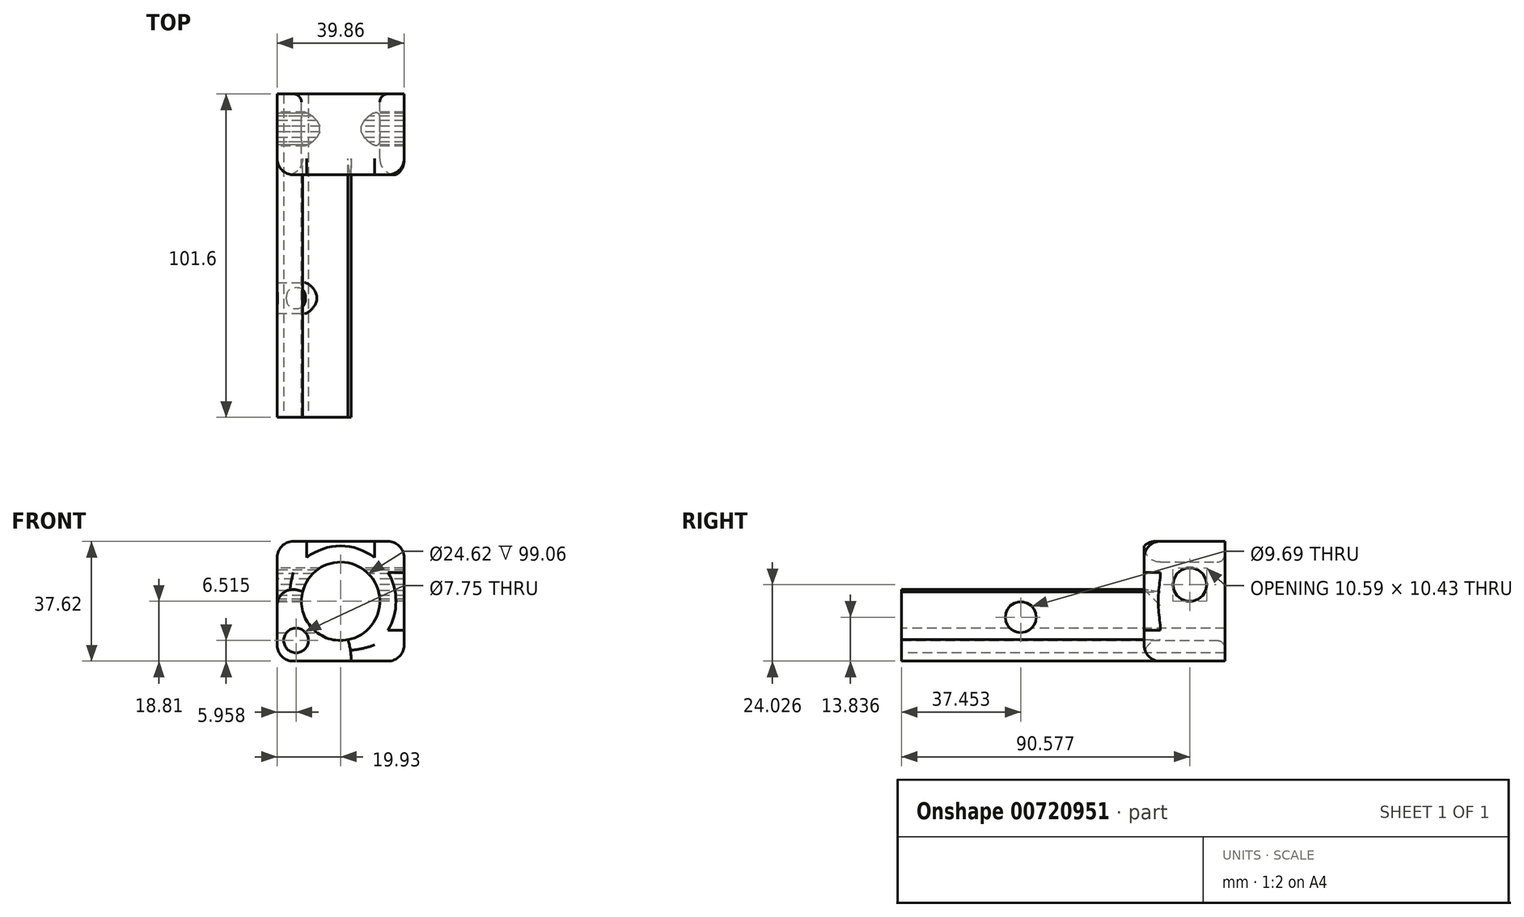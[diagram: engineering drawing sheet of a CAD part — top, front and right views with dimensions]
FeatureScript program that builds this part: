
annotation { "Feature Type Name" : "Feature", "Feature Type Description" : "" }
export const myFeature = defineFeature(function(context is Context, id is Id, definition is map)
    precondition{}
    {
        {
            var Q0;
            Q0=qCreatedBy(makeId("Front.planeOp"),FACE);
            var sketch = newSketch(context, id + "F0", { "sketchPlane" : qUnion([Q0])});
            skCircle(sketch, "E0", {"center": v(0, 0) * mm, "radius": 12.3 * mm});
            skLineSegment(sketch, "E1.bottom", {"start": v(-19.93, 18.81) * mm, "end": v(19.93, 18.81) * mm});
            skLineSegment(sketch, "E1.top", {"start": v(-19.93, -18.81) * mm, "end": v(19.93, -18.81) * mm});
            skLineSegment(sketch, "E1.left", {"start": v(-19.93, 18.81) * mm, "end": v(-19.93, -18.81) * mm});
            skLineSegment(sketch, "E1.right", {"start": v(19.93, 18.81) * mm, "end": v(19.93, -18.81) * mm});
            skCircle(sketch, "E2", {"center": v(-19.93, -18.81) * mm, "radius": 23.26 * mm});
            skSolve(sketch);
        }
        {
            var Q0;
            Q0=makeQuery(id+"F0.imprint","IMPRINT",FACE,{"disambiguationData":[TD([[makeQuery(id+"F0.imprint","IMPRINT",EDGE,{"derivedFrom":sQuery(id+"F0.wireOp",EDGE,"E0")}),-1.0]])]});
            extrude(context, id + "F1", {"entities" : qUnion([Q0]), "depth" : 101.6 * mm, "offsetDistance" : 25.4 * mm});
        }
        {
            var Q0;
            {var subQ1=sQuery(id+"F0.wireOp",EDGE,"E1.bottom");Q0=makeQuery(id+"F0.imprint","IMPRINT",FACE,{"disambiguationData":[TD([[makeQuery(id+"F0.imprint","IMPRINT",EDGE,{"derivedFrom":subQ1}),-1.0]])]});}
            extrude(context, id + "F2", {"entities" : qUnion([Q0]), "operationType" : NewBodyOperationType.ADD, "depth" : 25.4 * mm, "offsetDistance" : 25.4 * mm});
        }
        {
            var Q0;
            Q0=makeQuery(id+"F2.opExtrude","SWEPT_EDGE",EDGE,{"disambiguationData":[OSD([sQuery(id+"F0.wireOp",EDGE,"E1.bottom"),sQuery(id+"F0.wireOp",EDGE,"E1.left")])]});
            var Q1;
            Q1=makeQuery(id+"F1.opExtrude","SWEPT_EDGE",EDGE,{"disambiguationData":[OSD([sQuery(id+"F0.wireOp",EDGE,"E1.top"),sQuery(id+"F0.wireOp",EDGE,"E1.left")])]});
            var Q2;
            Q2=makeQuery(id+"F2.opExtrude","SWEPT_EDGE",EDGE,{"disambiguationData":[OSD([sQuery(id+"F0.wireOp",EDGE,"E1.top"),sQuery(id+"F0.wireOp",EDGE,"E1.right")])]});
            var Q3;
            Q3=makeQuery(id+"F2.opExtrude","SWEPT_EDGE",EDGE,{"disambiguationData":[OSD([sQuery(id+"F0.wireOp",EDGE,"E1.bottom"),sQuery(id+"F0.wireOp",EDGE,"E1.right")])]});
            fillet(context, id + "F3", {"entities" : qUnion([Q0, Q1, Q2, Q3]), "radius" : 5.08 * mm, "tangentPropagation" : true, "allowEdgeOverflow" : false});
        }
        {
            var Q0;
            Q0=qCreatedBy(makeId("Right.planeOp"),FACE);
            var sketch = newSketch(context, id + "F4", { "sketchPlane" : qUnion([Q0])});
            skCircle(sketch, "E3", {"center": v(-64.15, -4.97) * mm, "radius": 4.84 * mm});
            skSolve(sketch);
        }
        {
            var Q0;
            Q0 = qSketchRegion(id + "F4", true);
            extrude(context, id + "F5", {"entities" : qUnion([Q0]), "operationType" : NewBodyOperationType.REMOVE, "oppositeDirection" : true, "depth" : 25.4 * mm, "offsetDistance" : 25.4 * mm});
        }
        {
            var Q0;
            Q0=qCreatedBy(makeId("Front.planeOp"),FACE);
            var sketch = newSketch(context, id + "F6", { "sketchPlane" : qUnion([Q0])});
            skCircle(sketch, "E4", {"center": v(-13.97, -12.3) * mm, "radius": 3.88 * mm});
            skSolve(sketch);
        }
        {
            var Q0;
            Q0 = qSketchRegion(id + "F6", true);
            extrude(context, id + "F7", {"entities" : qUnion([Q0]), "operationType" : NewBodyOperationType.REMOVE, "oppositeDirection" : true, "depth" : 254 * mm, "offsetDistance" : 25.4 * mm, "hasSecondDirection" : true, "secondDirectionOppositeDirection" : false, "secondDirectionDepth" : 254 * mm});
        }
        {
            var Q0;
            Q0=makeQuery(id+"F2.opExtrude","CAP_EDGE",EDGE,{"disambiguationData":[OSD([sQuery(id+"F0.wireOp",EDGE,"E0")])],"isStart":false});
            fillet(context, id + "F8", {"entities" : qUnion([Q0]), "radius" : 5.08 * mm, "tangentPropagation" : true, "allowEdgeOverflow" : false});
        }
        {
            var Q0;
            {var subQ0=sQuery(id+"F0.wireOp",EDGE,"E0");Q0=makeQuery(id+"F2.boolean.opBoolean","MERGE",EDGE,{"derivedFrom":[makeQuery(id+"F1.opExtrude","CAP_EDGE",EDGE,{"disambiguationData":[OSD([subQ0])],"isStart":true}),makeQuery(id+"F2.opExtrude","CAP_EDGE",EDGE,{"disambiguationData":[OSD([subQ0])],"isStart":true})]});}
            fillet(context, id + "F9", {"entities" : qUnion([Q0]), "radius" : 2.54 * mm, "tangentPropagation" : true, "allowEdgeOverflow" : false});
        }
        {
            var Q0;
            Q0=makeQuery(id+"F1.opExtrude","SWEPT_EDGE",EDGE,{"disambiguationData":[OSD([sQuery(id+"F0.wireOp",EDGE,"E1.left"),sQuery(id+"F0.wireOp",EDGE,"E2")])]});
            fillet(context, id + "F10", {"entities" : qUnion([Q0]), "radius" : 5.08 * mm, "tangentPropagation" : true, "allowEdgeOverflow" : false});
        }
        {
            var Q0;
            Q0=qCreatedBy(makeId("Right.planeOp"),FACE);
            var sketch = newSketch(context, id + "F11", { "sketchPlane" : qUnion([Q0])});
            skCircle(sketch, "E5.cCircle", {"center": v(-11.02, 5.22) * mm, "radius": 5.22 * mm, "construction": true});
            skLineSegment(sketch, "E5.0", {"start": v(-10.1, 0) * mm, "end": v(-11.94, 0) * mm});
            skLineSegment(sketch, "E5.1", {"start": v(-11.94, 0) * mm, "end": v(-13.67, 0.63) * mm});
            skLineSegment(sketch, "E5.2", {"start": v(-13.67, 0.63) * mm, "end": v(-15.08, 1.81) * mm});
            skLineSegment(sketch, "E5.3", {"start": v(-15.08, 1.81) * mm, "end": v(-16, 3.4) * mm});
            skLineSegment(sketch, "E5.4", {"start": v(-16, 3.4) * mm, "end": v(-16.32, 5.22) * mm});
            skLineSegment(sketch, "E5.5", {"start": v(-16.32, 5.22) * mm, "end": v(-16, 7.03) * mm});
            skLineSegment(sketch, "E5.6", {"start": v(-16, 7.03) * mm, "end": v(-15.08, 8.62) * mm});
            skLineSegment(sketch, "E5.7", {"start": v(-15.08, 8.62) * mm, "end": v(-13.67, 9.8) * mm});
            skLineSegment(sketch, "E5.8", {"start": v(-13.67, 9.8) * mm, "end": v(-11.94, 10.43) * mm});
            skLineSegment(sketch, "E5.9", {"start": v(-11.94, 10.43) * mm, "end": v(-10.1, 10.43) * mm});
            skLineSegment(sketch, "E5.10", {"start": v(-10.1, 10.43) * mm, "end": v(-8.38, 9.8) * mm});
            skLineSegment(sketch, "E5.11", {"start": v(-8.38, 9.8) * mm, "end": v(-6.97, 8.62) * mm});
            skLineSegment(sketch, "E5.12", {"start": v(-6.97, 8.62) * mm, "end": v(-6.05, 7.03) * mm});
            skLineSegment(sketch, "E5.13", {"start": v(-6.05, 7.03) * mm, "end": v(-5.73, 5.22) * mm});
            skLineSegment(sketch, "E5.14", {"start": v(-5.73, 5.22) * mm, "end": v(-6.05, 3.4) * mm});
            skLineSegment(sketch, "E5.15", {"start": v(-6.05, 3.4) * mm, "end": v(-6.97, 1.81) * mm});
            skLineSegment(sketch, "E5.16", {"start": v(-6.97, 1.81) * mm, "end": v(-8.38, 0.63) * mm});
            skLineSegment(sketch, "E5.17", {"start": v(-8.38, 0.63) * mm, "end": v(-10.1, 0) * mm});
            skPoint(sketch, "E5.0.midPoint", {"position": v(-11.02, 0) * mm});
            skSolve(sketch);
        }
        {
            var Q0;
            Q0 = qSketchRegion(id + "F11", true);
            extrude(context, id + "F12", {"entities" : qUnion([Q0]), "operationType" : NewBodyOperationType.REMOVE, "depth" : 254 * mm, "offsetDistance" : 25.4 * mm, "hasSecondDirection" : true, "secondDirectionOppositeDirection" : true, "secondDirectionDepth" : 25.4 * mm});
        }
        {
            var Q0;
            Q0=makeQuery(id+"F2.opExtrude","CAP_EDGE",EDGE,{"disambiguationData":[OSD([sQuery(id+"F0.wireOp",EDGE,"E1.bottom")])],"isStart":false});
            fillet(context, id + "F13", {"entities" : qUnion([Q0]), "radius" : 5.08 * mm, "tangentPropagation" : true, "allowEdgeOverflow" : false});
        }
    });
